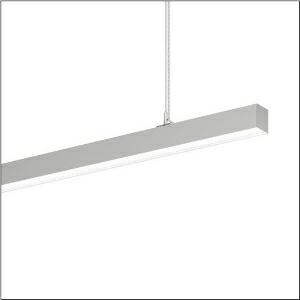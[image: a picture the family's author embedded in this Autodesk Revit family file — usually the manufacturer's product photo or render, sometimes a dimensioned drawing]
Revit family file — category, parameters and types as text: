
# Revit family: silica_21_51mx30dc39sb
name_source: partatom
category: Lighting Fixtures
units: mm (PartAtom-declared; Revit-internal decimal feet)

## family parameters
Cut with Voids When Loaded = No
Host = Face
Light Source = No
Part Type = Normal
Room Calculation Point = No
Round Connector Dimension = Use Diameter
Shared = No

## types (1)
- --- (1 x LED, 10520 lm, 68.3 W, 3000K)
    Apparent Load = 68 VA
    CIE Flux Codes = 47 79 96 57 100
    Color Rendering = 80
    Color Temperature = 3000K
    Default Elevation = 1800 mm
    Description = Silica 21, office luminaire, primary optical cover: cover, of PMMA, opal, light emission: direct/indirect distribution, primary light characteristic: symmetric, installation type: suspended mounting, LED, rated luminous flux: 10.520lm, luminous efficacy: 154lm/W, light colour: 830, colour temperature: 3000K, control gear: DALI 2, with terminal, 3+2-pole, max. 2.5mm², mains connection: 220..240V, AC, 50/60Hz, rated input power: 68.3W, luminaire housing, of aluminium, metallic grey (RAL 9006), length: 3.004mm, width: 53mm, height: 53mm, protection rating (complete): IP20, insulation class (complete): insulation class I (protective earthing), certification: CE, permissible operating ambient temperature: 0..+35°C, standard: EN 50419, packaging unit: 1 piece
    Height = 53 mm
    Lamp = 1 x LED
    Lamp Light Flux = 10520 lm
    Lamp Power = 68.3 W
    Lamp count = 1
    Length = 3004 mm
    Luminous efficacy = 154 lm/W
    Manufacturer = Siteco
    ModVariant = No
    Model = 51MX30DC39SB
    Mounting Place = Ceiling
    Mounting Type = Pendant
    Number of Poles = 1
    OnlyDefault = Yes
    Power Factor = 1
    Product Name = Silica 21
    Product group = office luminaire | ceiling pendant
    ProductGroupID = 903
    Protection Class = Protection class I
    Protection Degree = IP 20
    RLX_Detail_Level = 1
    RLX_Emergency_Light_Flux = 0 lm
    RLX_Emergency_Type = 0
    RLX_Emergency_Type_DB = No
    RlxData = <blob elided: 23409 chars, md5=3c015018>
    Socket = socket
    Standby Power = 0 W
    System Light Flux = 10520 lm
    System Power = 68 W
    Type Comments = factory setting: luminous flux: 100 % | dim-lin: 254 | 233 mA
    Type Image = l_1335864.jpg
    URL = http://relux.com
    VarID = @adj_117229
    Voltage = 0 V
    Weight = 0.00 kg
    Width = 53 mm

## geometry (parser evidence)
native form markers: Blend x4, Sweep x14
no freeform markers — native parametric forms only
